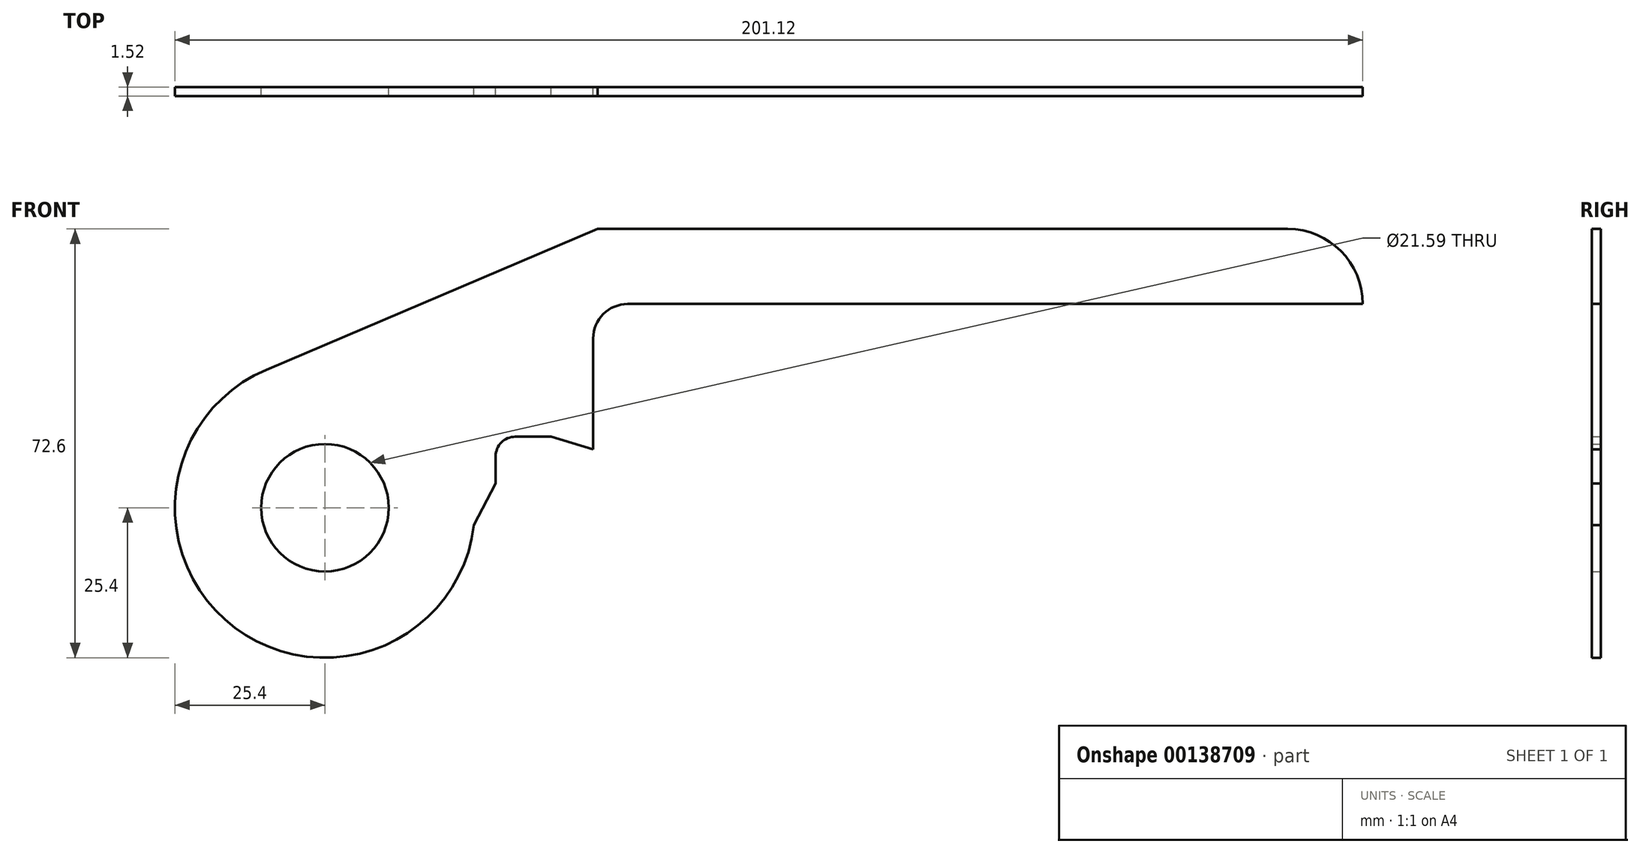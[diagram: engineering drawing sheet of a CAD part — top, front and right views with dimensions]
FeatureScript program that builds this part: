
annotation { "Feature Type Name" : "Feature", "Feature Type Description" : "" }
export const myFeature = defineFeature(function(context is Context, id is Id, definition is map)
    precondition{}
    {
        {
            var Q0;
            Q0=qCreatedBy(makeId("Front.planeOp"),FACE);
            var sketch = newSketch(context, id + "F0", { "sketchPlane" : qUnion([Q0])});
            skCircle(sketch, "E0", {"center": v(0, 0) * mm, "radius": 25.4 * mm});
            skLineSegment(sketch, "E1", {"start": v(-9.92, 23.38) * mm, "end": v(46.19, 47.2) * mm});
            skLineSegment(sketch, "E2", {"start": v(51.26, 34.5) * mm, "end": v(175.72, 34.5) * mm});
            skLineSegment(sketch, "E3", {"start": v(46.19, 47.2) * mm, "end": v(163.02, 47.2) * mm});
            skArc(sketch, "E4", {"start": v(175.72, 34.5) * mm, "mid": v(172, 43.48) * mm, "end": v(163.02, 47.2) * mm});
            skArc(sketch, "E5", {"start": v(51.26, 34.5) * mm, "mid": v(47.13, 32.79) * mm, "end": v(45.42, 28.66) * mm});
            skLineSegment(sketch, "E6", {"start": v(45.42, 28.66) * mm, "end": v(45.42, 9.86) * mm});
            skLineSegment(sketch, "E7", {"start": v(45.42, 9.86) * mm, "end": v(38.3, 12.02) * mm});
            skLineSegment(sketch, "E8", {"start": v(38.3, 12.02) * mm, "end": v(32.21, 12.02) * mm});
            skArc(sketch, "E9", {"start": v(32.21, 12.02) * mm, "mid": v(29.88, 11.05) * mm, "end": v(28.9, 8.72) * mm});
            skLineSegment(sketch, "E10", {"start": v(28.9, 8.72) * mm, "end": v(28.9, 4.1) * mm});
            skLineSegment(sketch, "E11", {"start": v(28.9, 4.1) * mm, "end": v(25.23, -2.97) * mm});
            skCircle(sketch, "E12", {"center": v(0, 0) * mm, "radius": 10.8 * mm});
            skSolve(sketch);
        }
        {
            var Q0;
            {var subQ0=sQuery(id+"F0.wireOp",EDGE,"E0");var subQ1=makeQuery(id+"F0.imprint","INTERSECT",VERTEX,{"derivedFrom":[subQ0,sQuery(id+"F0.wireOp",EDGE,"E1")]});Q0=makeQuery(id+"F0.imprint","IMPRINT",FACE,{"disambiguationData":[TD([[makeQuery(id+"F0.imprint","IMPRINT",EDGE,{"disambiguationData":[TD([[subQ1,-1.0]])],"derivedFrom":subQ0}),1.0]])]});}
            var Q1;
            {var subQ0=sQuery(id+"F0.wireOp",EDGE,"E1");Q1=makeQuery(id+"F0.imprint","IMPRINT",FACE,{"disambiguationData":[TD([[makeQuery(id+"F0.imprint","IMPRINT",EDGE,{"derivedFrom":subQ0}),-1.0]])]});}
            extrude(context, id + "F1", {"entities" : qUnion([Q0, Q1]), "depth" : 1.52 * mm});
        }
    });
